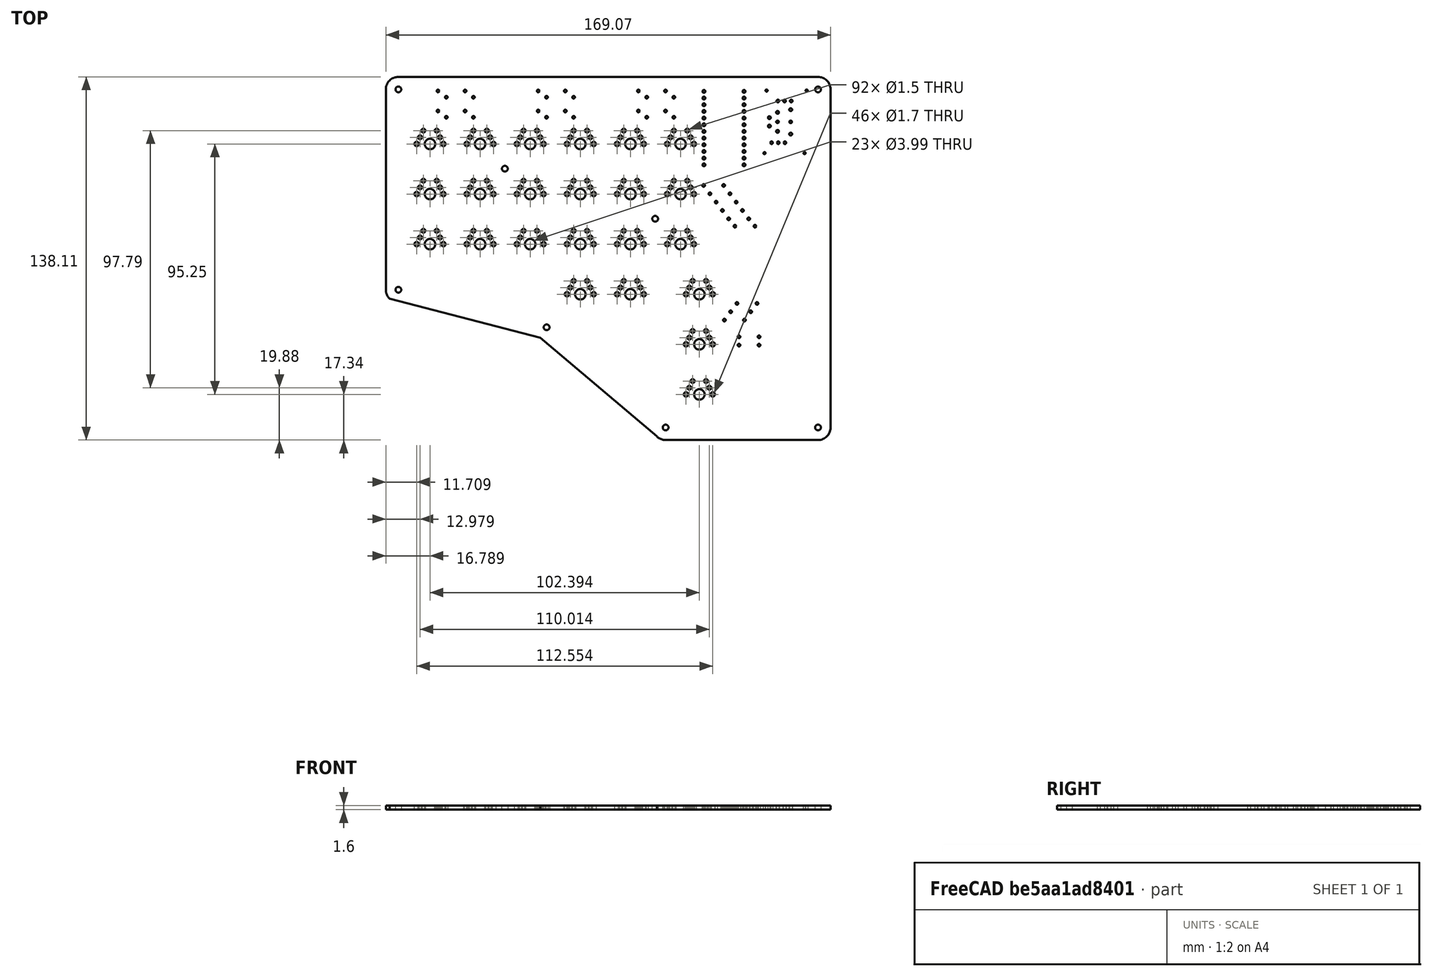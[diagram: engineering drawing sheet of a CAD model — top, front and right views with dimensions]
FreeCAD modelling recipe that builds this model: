
FCSTD DOCUMENT  (FreeCAD 0.19R24267 +148 (Git))
Label: parametric.model.experiment
License: All rights reserved
LicenseURL: http://en.wikipedia.org/wiki/All_rights_reserved
objects: App::Part×4, Sketcher::SketchObject×2, PartDesign::CoordinateSystem×1, Part::Feature×1, PartDesign::Body×1
note: 5 computed .brp shape members not serialized (recipe doc carries the construction recipe); baked Part::Feature solids carry a one-line shape summary decoded from their .brp

FEATURE [PartDesign::CoordinateSystem] Local_CS_c5df
  AttacherType = Attacher::AttachEngine3D
FEATURE [Part::Feature] Pcb_c5df
  Placement = pos=(-21.48,22.9996,0) rot=(0,0,1;0rad)
  shape: bbox 169.1 x 138.1 x 1.6 mm, 270 faces (baked)
FEATURE [Sketcher::SketchObject] PCB_Sketch_c5df
  FullyConstrained = true
  sketch-geometry (11):
    g0: LineSegment StartX=164.25 StartY=2.5e-15 StartZ=0 EndX=164.25 EndY=-128.5 EndZ=0
    g1: LineSegment StartX=54.0843 StartY=-94.6132 StartZ=0 EndX=-1.16741 EndY=-80.6043 EndZ=0
    g2: LineSegment StartX=-4.75 StartY=-1e-15 StartZ=0 EndX=-4.75 EndY=-76 EndZ=0
    g3: LineSegment StartX=-1.3e-15 StartY=4.75 StartZ=0 EndX=159.5 EndY=4.75 EndZ=0
    g4: LineSegment StartX=159.5 StartY=-133.25 StartZ=0 EndX=101.5 EndY=-133.25 EndZ=0
    g5: LineSegment StartX=54.0843 StartY=-94.6132 StartZ=0 EndX=98.4323 EndY=-132.127 EndZ=0
    g6: ArcOfCircle CenterX=0 CenterY=0 CenterZ=0 NormalX=0 NormalY=0 NormalZ=-1 AngleXU=3.25477e-08 Radius=4.75 StartAngle=6.28319 EndAngle=7.85398
    g7: ArcOfCircle CenterX=101.5 CenterY=-128.5 CenterZ=0 NormalX=0 NormalY=0 NormalZ=-1 AngleXU=-1.5708 Radius=4.75 StartAngle=6.28319 EndAngle=6.98529
    g8: ArcOfCircle CenterX=159.5 CenterY=0 CenterZ=0 NormalX=0 NormalY=0 NormalZ=-1 AngleXU=1.5708 Radius=4.75 StartAngle=6.28319 EndAngle=7.85398
    g9: ArcOfCircle CenterX=0 CenterY=-76 CenterZ=0 NormalX=0 NormalY=0 NormalZ=-1 AngleXU=-0.785398 Radius=4.75 StartAngle=5.7461 EndAngle=7.06858
    g10: ArcOfCircle CenterX=159.5 CenterY=-128.5 CenterZ=0 NormalX=0 NormalY=0 NormalZ=-1 AngleXU=-3.14159 Radius=4.75 StartAngle=6.28319 EndAngle=7.85398
  constraints (27):
    c: Coincident(g1,g5)
    c: Tangent(g3,g6) = 1.5708
    c: Horizontal(g3)
    c: Tangent(g3,g8) = 1.5708
    c: Tangent(g0,g8) = 1.5708
    c: Perpendicular(g3,g0)
    c: Tangent(g0,g10) = 1.5708
    c: Tangent(g4,g10) = 1.5708
    c: Tangent(g4,g7) = 1.5708
    c: Tangent(g5,g7) = -1.5708
    c: Perpendicular(g0,g4)
    c: Tangent(g1,g9) = 1.5708
    c: Tangent(g2,g9) = -1.5708
    c: Perpendicular(g3,g2)
    c: Equal(g7,g8)
    c: Equal(g7,g9)
    c: Equal(g7,g10)
    c: Radius(g7) = 4.75
    c: Tangent(g2,g6) = -1.5708
    c: DistanceX(g2,g0) = 169
    c: DistanceY(g4,g3) = 138
    c: DistanceX(g4,g4) = 58
    c: Radius(g6) = 4.75
    c: Coincident(g6,g-1)
    c: DistanceY(g2,g2) = 76
    c: Angle(g1,g5) = 2.68781
    c: Distance(g1) = 57
FEATURE [App::Part] Board_Geoms_c5df
  Group = -> [Local_CS_c5df,Pcb_c5df,PCB_Sketch_c5df]
  Origin = -> Origin
FEATURE [App::Part] Step_Models_c5df
  Origin = -> Origin002
FEATURE [App::Part] Board_c5df  label="pcb"
  Group = -> [Board_Geoms_c5df,Step_Models_c5df]
  Origin = -> Origin001
FEATURE [Sketcher::SketchObject] Sketch003
  FullyConstrained = false
  sketch-geometry (223):
    g0: Circle CenterX=0 CenterY=6e-16 CenterZ=0 NormalX=0 NormalY=0 NormalZ=1 AngleXU=0 Radius=1.1
    g1: Circle CenterX=159.5 CenterY=6e-16 CenterZ=0 NormalX=0 NormalY=0 NormalZ=1 AngleXU=0 Radius=1.1
    g2: LineSegment StartX=3e-16 StartY=4.75 StartZ=0 EndX=159.5 EndY=4.75 EndZ=0
    g3: ArcOfCircle CenterX=159.5 CenterY=-4e-16 CenterZ=0 NormalX=0 NormalY=0 NormalZ=1 AngleXU=0 Radius=4.75 StartAngle=1e-16 EndAngle=1.5708
    g4: LineSegment StartX=164.25 StartY=6e-16 StartZ=0 EndX=164.25 EndY=-128.5 EndZ=0
    g5: Circle CenterX=159.5 CenterY=-128.5 CenterZ=0 NormalX=0 NormalY=0 NormalZ=1 AngleXU=0 Radius=1.1
    g6: ArcOfCircle CenterX=159.5 CenterY=-128.5 CenterZ=0 NormalX=0 NormalY=0 NormalZ=1 AngleXU=0 Radius=4.75 StartAngle=4.71239 EndAngle=6.28319
    g7: LineSegment StartX=159.5 StartY=-133.25 StartZ=0 EndX=101.5 EndY=-133.25 EndZ=0
    g8: Circle CenterX=101.5 CenterY=-128.5 CenterZ=0 NormalX=0 NormalY=0 NormalZ=1 AngleXU=0 Radius=1.1
    g9: ArcOfCircle CenterX=101.5 CenterY=-128.5 CenterZ=0 NormalX=0 NormalY=0 NormalZ=1 AngleXU=0 Radius=4.75 StartAngle=4.01077 EndAngle=4.71239
    g10: LineSegment StartX=98.4341 StartY=-132.128 StartZ=0 EndX=53.9755 EndY=-94.5576 EndZ=0
    g11: LineSegment StartX=53.9755 StartY=-94.5576 StartZ=0 EndX=-1.16521 EndY=-80.6049 EndZ=0
    g12: ArcOfCircle CenterX=9.3e-15 CenterY=-76 CenterZ=0 NormalX=0 NormalY=0 NormalZ=1 AngleXU=0 Radius=4.75 StartAngle=3.14159 EndAngle=4.46455
    g13: LineSegment StartX=-4.75 StartY=-76 StartZ=0 EndX=-4.75 EndY=0 EndZ=0
    g14: LineSegment StartX=5.54 StartY=-13.74 StartZ=0 EndX=18.54 EndY=-13.74 EndZ=0
    g15: LineSegment StartX=5.54 StartY=-27.74 StartZ=0 EndX=18.54 EndY=-27.74 EndZ=0
    g16: LineSegment StartX=5.04 StartY=-14.24 StartZ=0 EndX=5.04 EndY=-27.24 EndZ=0
    g17: LineSegment StartX=19.04 StartY=-14.24 StartZ=0 EndX=19.04 EndY=-27.24 EndZ=0
    g18: ArcOfCircle CenterX=5.54 CenterY=-14.24 CenterZ=0 NormalX=0 NormalY=0 NormalZ=1 AngleXU=0 Radius=0.5 StartAngle=1.5708 EndAngle=3.14159
    g19: ArcOfCircle CenterX=18.54 CenterY=-27.24 CenterZ=0 NormalX=0 NormalY=0 NormalZ=1 AngleXU=0 Radius=0.5 StartAngle=4.71239 EndAngle=6.28319
    g20: LineSegment StartX=24.59 StartY=-13.74 StartZ=0 EndX=37.59 EndY=-13.74 EndZ=0
    g21: LineSegment StartX=24.59 StartY=-27.74 StartZ=0 EndX=37.59 EndY=-27.74 EndZ=0
    g22: LineSegment StartX=24.09 StartY=-14.24 StartZ=0 EndX=24.09 EndY=-27.24 EndZ=0
    g23: LineSegment StartX=38.09 StartY=-14.24 StartZ=0 EndX=38.09 EndY=-27.24 EndZ=0
    g24: ArcOfCircle CenterX=24.59 CenterY=-14.24 CenterZ=0 NormalX=0 NormalY=0 NormalZ=1 AngleXU=0 Radius=0.5 StartAngle=1.5708 EndAngle=3.14159
    g25: ArcOfCircle CenterX=24.59 CenterY=-27.24 CenterZ=0 NormalX=0 NormalY=0 NormalZ=1 AngleXU=0 Radius=0.5 StartAngle=3.14159 EndAngle=4.71239
    g26: LineSegment StartX=5.54 StartY=-32.79 StartZ=0 EndX=18.54 EndY=-32.79 EndZ=0
    g27: LineSegment StartX=5.54 StartY=-46.79 StartZ=0 EndX=18.54 EndY=-46.79 EndZ=0
    g28: LineSegment StartX=5.04 StartY=-33.29 StartZ=0 EndX=5.04 EndY=-46.29 EndZ=0
    g29: LineSegment StartX=19.04 StartY=-33.29 StartZ=0 EndX=19.04 EndY=-46.29 EndZ=0
    g30: ArcOfCircle CenterX=18.54 CenterY=-33.29 CenterZ=0 NormalX=0 NormalY=0 NormalZ=1 AngleXU=0 Radius=0.5 StartAngle=6.341e-13 EndAngle=1.5708
    g31: LineSegment StartX=24.59 StartY=-32.79 StartZ=0 EndX=37.59 EndY=-32.79 EndZ=0
    g32: LineSegment StartX=24.59 StartY=-46.79 StartZ=0 EndX=37.59 EndY=-46.79 EndZ=0
    g33: LineSegment StartX=24.09 StartY=-33.29 StartZ=0 EndX=24.09 EndY=-46.29 EndZ=0
    g34: LineSegment StartX=38.09 StartY=-33.29 StartZ=0 EndX=38.09 EndY=-46.29 EndZ=0
    g35: ArcOfCircle CenterX=24.59 CenterY=-33.29 CenterZ=0 NormalX=0 NormalY=0 NormalZ=1 AngleXU=0 Radius=0.5 StartAngle=1.5708 EndAngle=3.14159
    g36: ArcOfCircle CenterX=37.59 CenterY=-46.29 CenterZ=0 NormalX=0 NormalY=0 NormalZ=1 AngleXU=0 Radius=0.5 StartAngle=4.71239 EndAngle=6.28319
    g37: ArcOfCircle CenterX=18.54 CenterY=-14.24 CenterZ=0 NormalX=0 NormalY=0 NormalZ=1 AngleXU=0 Radius=0.5 StartAngle=9e-16 EndAngle=1.5708
    g38: ArcOfCircle CenterX=37.59 CenterY=-14.24 CenterZ=0 NormalX=0 NormalY=0 NormalZ=1 AngleXU=0 Radius=0.5 StartAngle=-9e-16 EndAngle=1.5708
    g39: ArcOfCircle CenterX=37.59 CenterY=-33.29 CenterZ=0 NormalX=0 NormalY=0 NormalZ=1 AngleXU=0 Radius=0.5 StartAngle=-1.692e-12 EndAngle=1.5708
    g40: ArcOfCircle CenterX=24.59 CenterY=-46.29 CenterZ=0 NormalX=0 NormalY=0 NormalZ=1 AngleXU=0 Radius=0.5 StartAngle=3.14159 EndAngle=4.71239
    g41: ArcOfCircle CenterX=18.54 CenterY=-46.29 CenterZ=0 NormalX=0 NormalY=0 NormalZ=1 AngleXU=0 Radius=0.5 StartAngle=4.71239 EndAngle=6.28319
    g42: ArcOfCircle CenterX=5.54 CenterY=-46.29 CenterZ=0 NormalX=0 NormalY=0 NormalZ=1 AngleXU=0 Radius=0.5 StartAngle=3.14159 EndAngle=4.71239
    g43: ArcOfCircle CenterX=5.54 CenterY=-33.29 CenterZ=0 NormalX=0 NormalY=0 NormalZ=1 AngleXU=0 Radius=0.5 StartAngle=1.5708 EndAngle=3.14159
    g44: ArcOfCircle CenterX=5.54 CenterY=-27.24 CenterZ=0 NormalX=0 NormalY=0 NormalZ=1 AngleXU=0 Radius=0.5 StartAngle=3.14159 EndAngle=4.71239
    g45: LineSegment StartX=43.64 StartY=-13.74 StartZ=0 EndX=56.64 EndY=-13.74 EndZ=0
    g46: LineSegment StartX=43.64 StartY=-27.74 StartZ=0 EndX=56.64 EndY=-27.74 EndZ=0
    g47: LineSegment StartX=43.14 StartY=-14.24 StartZ=0 EndX=43.14 EndY=-27.24 EndZ=0
    g48: LineSegment StartX=57.14 StartY=-14.24 StartZ=0 EndX=57.14 EndY=-27.24 EndZ=0
    g49: ArcOfCircle CenterX=43.64 CenterY=-14.24 CenterZ=0 NormalX=0 NormalY=0 NormalZ=1 AngleXU=0 Radius=0.5 StartAngle=1.5708 EndAngle=3.14159
    g50: ArcOfCircle CenterX=56.64 CenterY=-27.24 CenterZ=0 NormalX=0 NormalY=0 NormalZ=1 AngleXU=0 Radius=0.5 StartAngle=4.71239 EndAngle=6.28319
    g51: LineSegment StartX=62.69 StartY=-13.74 StartZ=0 EndX=75.69 EndY=-13.74 EndZ=0
    g52: LineSegment StartX=62.69 StartY=-27.74 StartZ=0 EndX=75.69 EndY=-27.74 EndZ=0
    g53: LineSegment StartX=62.19 StartY=-14.24 StartZ=0 EndX=62.19 EndY=-27.24 EndZ=0
    g54: LineSegment StartX=76.19 StartY=-14.24 StartZ=0 EndX=76.19 EndY=-27.24 EndZ=0
    g55: ArcOfCircle CenterX=62.69 CenterY=-14.24 CenterZ=0 NormalX=0 NormalY=0 NormalZ=1 AngleXU=0 Radius=0.5 StartAngle=1.5708 EndAngle=3.14159
    g56: ArcOfCircle CenterX=62.69 CenterY=-27.24 CenterZ=0 NormalX=0 NormalY=0 NormalZ=1 AngleXU=0 Radius=0.5 StartAngle=3.14159 EndAngle=4.71239
    g57: LineSegment StartX=43.64 StartY=-32.79 StartZ=0 EndX=56.64 EndY=-32.79 EndZ=0
    g58: LineSegment StartX=43.64 StartY=-46.79 StartZ=0 EndX=56.64 EndY=-46.79 EndZ=0
    g59: LineSegment StartX=43.14 StartY=-33.29 StartZ=0 EndX=43.14 EndY=-46.29 EndZ=0
    g60: LineSegment StartX=57.14 StartY=-33.29 StartZ=0 EndX=57.14 EndY=-46.29 EndZ=0
    g61: ArcOfCircle CenterX=56.64 CenterY=-33.29 CenterZ=0 NormalX=0 NormalY=0 NormalZ=1 AngleXU=0 Radius=0.5 StartAngle=-1.252e-13 EndAngle=1.5708
    g62: LineSegment StartX=62.69 StartY=-32.79 StartZ=0 EndX=75.69 EndY=-32.79 EndZ=0
    g63: LineSegment StartX=62.69 StartY=-46.79 StartZ=0 EndX=75.69 EndY=-46.79 EndZ=0
    g64: LineSegment StartX=62.19 StartY=-33.29 StartZ=0 EndX=62.19 EndY=-46.29 EndZ=0
    g65: LineSegment StartX=76.19 StartY=-33.29 StartZ=0 EndX=76.19 EndY=-46.29 EndZ=0
    g66: ArcOfCircle CenterX=62.69 CenterY=-33.29 CenterZ=0 NormalX=0 NormalY=0 NormalZ=1 AngleXU=0 Radius=0.5 StartAngle=1.5708 EndAngle=3.14159
    g67: ArcOfCircle CenterX=75.69 CenterY=-46.29 CenterZ=0 NormalX=0 NormalY=0 NormalZ=1 AngleXU=0 Radius=0.5 StartAngle=4.71239 EndAngle=6.28319
    g68: ArcOfCircle CenterX=56.64 CenterY=-14.24 CenterZ=0 NormalX=0 NormalY=0 NormalZ=1 AngleXU=0 Radius=0.5 StartAngle=-1.8e-15 EndAngle=1.5708
    g69: ArcOfCircle CenterX=75.69 CenterY=-14.24 CenterZ=0 NormalX=0 NormalY=0 NormalZ=1 AngleXU=0 Radius=0.5 StartAngle=1.8e-15 EndAngle=1.5708
    g70: ArcOfCircle CenterX=75.69 CenterY=-27.24 CenterZ=0 NormalX=0 NormalY=0 NormalZ=1 AngleXU=0 Radius=0.5 StartAngle=4.71239 EndAngle=6.28319
    g71: ArcOfCircle CenterX=75.69 CenterY=-33.29 CenterZ=0 NormalX=0 NormalY=0 NormalZ=1 AngleXU=0 Radius=0.5 StartAngle=0 EndAngle=1.5708
    g72: ArcOfCircle CenterX=62.69 CenterY=-46.29 CenterZ=0 NormalX=0 NormalY=0 NormalZ=1 AngleXU=0 Radius=0.5 StartAngle=3.14159 EndAngle=4.71239
    g73: ArcOfCircle CenterX=56.64 CenterY=-46.29 CenterZ=0 NormalX=0 NormalY=0 NormalZ=1 AngleXU=0 Radius=0.5 StartAngle=4.71239 EndAngle=6.28319
    g74: ArcOfCircle CenterX=43.64 CenterY=-46.29 CenterZ=0 NormalX=0 NormalY=0 NormalZ=1 AngleXU=0 Radius=0.5 StartAngle=3.14159 EndAngle=4.71239
    g75: ArcOfCircle CenterX=43.64 CenterY=-33.29 CenterZ=0 NormalX=0 NormalY=0 NormalZ=1 AngleXU=0 Radius=0.5 StartAngle=1.5708 EndAngle=3.14159
    g76: ArcOfCircle CenterX=43.64 CenterY=-27.24 CenterZ=0 NormalX=0 NormalY=0 NormalZ=1 AngleXU=0 Radius=0.5 StartAngle=3.14159 EndAngle=4.71239
    g77: LineSegment StartX=5.54 StartY=-51.84 StartZ=0 EndX=18.54 EndY=-51.84 EndZ=0
    g78: LineSegment StartX=5.54 StartY=-65.84 StartZ=0 EndX=18.54 EndY=-65.84 EndZ=0
    g79: LineSegment StartX=5.04 StartY=-52.34 StartZ=0 EndX=5.04 EndY=-65.34 EndZ=0
    g80: LineSegment StartX=19.04 StartY=-52.34 StartZ=0 EndX=19.04 EndY=-65.34 EndZ=0
    g81: ArcOfCircle CenterX=18.54 CenterY=-52.34 CenterZ=0 NormalX=0 NormalY=0 NormalZ=1 AngleXU=0 Radius=0.5 StartAngle=1.38282e-07 EndAngle=1.5708
    g82: LineSegment StartX=24.59 StartY=-51.84 StartZ=0 EndX=37.59 EndY=-51.84 EndZ=0
    g83: LineSegment StartX=24.59 StartY=-65.84 StartZ=0 EndX=37.59 EndY=-65.84 EndZ=0
    g84: LineSegment StartX=24.09 StartY=-52.34 StartZ=0 EndX=24.09 EndY=-65.34 EndZ=0
    g85: LineSegment StartX=38.09 StartY=-52.34 StartZ=0 EndX=38.09 EndY=-65.34 EndZ=0
    g86: ArcOfCircle CenterX=37.59 CenterY=-65.34 CenterZ=0 NormalX=0 NormalY=0 NormalZ=1 AngleXU=0 Radius=0.5 StartAngle=4.71239 EndAngle=6.28319
    g87: ArcOfCircle CenterX=24.59 CenterY=-65.34 CenterZ=0 NormalX=0 NormalY=0 NormalZ=1 AngleXU=0 Radius=0.5 StartAngle=3.14159 EndAngle=4.71239
    g88: ArcOfCircle CenterX=18.54 CenterY=-65.34 CenterZ=0 NormalX=0 NormalY=0 NormalZ=1 AngleXU=0 Radius=0.5 StartAngle=4.71239 EndAngle=6.28317
    g89: ArcOfCircle CenterX=5.54 CenterY=-65.34 CenterZ=0 NormalX=0 NormalY=0 NormalZ=1 AngleXU=0 Radius=0.5 StartAngle=3.14161 EndAngle=4.71239
    g90: ArcOfCircle CenterX=5.54 CenterY=-52.34 CenterZ=0 NormalX=0 NormalY=0 NormalZ=1 AngleXU=0 Radius=0.5 StartAngle=1.5708 EndAngle=3.14159
    g91: LineSegment StartX=43.64 StartY=-51.84 StartZ=0 EndX=56.64 EndY=-51.84 EndZ=0
    g92: LineSegment StartX=43.64 StartY=-65.84 StartZ=0 EndX=56.64 EndY=-65.84 EndZ=0
    g93: LineSegment StartX=43.14 StartY=-52.34 StartZ=0 EndX=43.14 EndY=-65.34 EndZ=0
    g94: LineSegment StartX=57.14 StartY=-52.34 StartZ=0 EndX=57.14 EndY=-65.34 EndZ=0
    g95: ArcOfCircle CenterX=56.64 CenterY=-52.34 CenterZ=0 NormalX=0 NormalY=0 NormalZ=1 AngleXU=0 Radius=0.5 StartAngle=1.73068e-05 EndAngle=1.5708
    g96: LineSegment StartX=62.69 StartY=-51.84 StartZ=0 EndX=75.69 EndY=-51.84 EndZ=0
    g97: LineSegment StartX=62.69 StartY=-65.84 StartZ=0 EndX=75.69 EndY=-65.84 EndZ=0
    g98: LineSegment StartX=62.19 StartY=-52.34 StartZ=0 EndX=62.19 EndY=-65.34 EndZ=0
    g99: LineSegment StartX=76.19 StartY=-52.34 StartZ=0 EndX=76.19 EndY=-65.34 EndZ=0
    g100: ArcOfCircle CenterX=62.69 CenterY=-52.34 CenterZ=0 NormalX=0 NormalY=0 NormalZ=1 AngleXU=0 Radius=0.5 StartAngle=1.5708 EndAngle=3.14158
    g101: ArcOfCircle CenterX=75.69 CenterY=-65.34 CenterZ=0 NormalX=0 NormalY=0 NormalZ=1 AngleXU=0 Radius=0.5 StartAngle=4.71239 EndAngle=6.28317
    g102: ArcOfCircle CenterX=62.69 CenterY=-65.34 CenterZ=0 NormalX=0 NormalY=0 NormalZ=1 AngleXU=0 Radius=0.5 StartAngle=3.14159 EndAngle=4.71239
    g103: ArcOfCircle CenterX=56.64 CenterY=-65.34 CenterZ=0 NormalX=0 NormalY=0 NormalZ=1 AngleXU=0 Radius=0.5 StartAngle=4.71239 EndAngle=6.28319
    g104: ArcOfCircle CenterX=43.64 CenterY=-65.34 CenterZ=0 NormalX=0 NormalY=0 NormalZ=1 AngleXU=0 Radius=0.5 StartAngle=3.14159 EndAngle=4.71239
    g105: ArcOfCircle CenterX=43.64 CenterY=-52.34 CenterZ=0 NormalX=0 NormalY=0 NormalZ=1 AngleXU=0 Radius=0.5 StartAngle=1.5708 EndAngle=3.14158
    g106: ArcOfCircle CenterX=24.59 CenterY=-52.34 CenterZ=0 NormalX=0 NormalY=0 NormalZ=1 AngleXU=0 Radius=0.5 StartAngle=1.5708 EndAngle=3.14158
    g107: ArcOfCircle CenterX=37.59 CenterY=-52.34 CenterZ=0 NormalX=0 NormalY=0 NormalZ=1 AngleXU=0 Radius=0.5 StartAngle=1.73068e-05 EndAngle=1.5708
    g108: LineSegment StartX=81.74 StartY=-13.74 StartZ=0 EndX=94.74 EndY=-13.74 EndZ=0
    g109: LineSegment StartX=81.74 StartY=-27.74 StartZ=0 EndX=94.74 EndY=-27.74 EndZ=0
    g110: LineSegment StartX=81.24 StartY=-14.24 StartZ=0 EndX=81.24 EndY=-27.24 EndZ=0
    g111: LineSegment StartX=95.24 StartY=-14.24 StartZ=0 EndX=95.24 EndY=-27.24 EndZ=0
    g112: ArcOfCircle CenterX=81.74 CenterY=-14.24 CenterZ=0 NormalX=0 NormalY=0 NormalZ=1 AngleXU=0 Radius=0.5 StartAngle=1.5708 EndAngle=3.14159
    g113: ArcOfCircle CenterX=94.74 CenterY=-27.24 CenterZ=0 NormalX=0 NormalY=0 NormalZ=1 AngleXU=0 Radius=0.5 StartAngle=4.71239 EndAngle=6.28319
    g114: LineSegment StartX=100.79 StartY=-13.74 StartZ=0 EndX=113.79 EndY=-13.74 EndZ=0
    g115: LineSegment StartX=100.79 StartY=-27.74 StartZ=0 EndX=113.79 EndY=-27.74 EndZ=0
    g116: LineSegment StartX=100.29 StartY=-14.24 StartZ=0 EndX=100.29 EndY=-27.24 EndZ=0
    g117: LineSegment StartX=114.29 StartY=-14.24 StartZ=0 EndX=114.29 EndY=-27.24 EndZ=0
    g118: ArcOfCircle CenterX=100.79 CenterY=-14.24 CenterZ=0 NormalX=0 NormalY=0 NormalZ=1 AngleXU=0 Radius=0.5 StartAngle=1.5708 EndAngle=3.14159
    g119: ArcOfCircle CenterX=100.79 CenterY=-27.24 CenterZ=0 NormalX=0 NormalY=0 NormalZ=1 AngleXU=0 Radius=0.5 StartAngle=3.14159 EndAngle=4.71239
    g120: LineSegment StartX=81.74 StartY=-32.79 StartZ=0 EndX=94.74 EndY=-32.79 EndZ=0
    g121: LineSegment StartX=81.74 StartY=-46.79 StartZ=0 EndX=94.74 EndY=-46.79 EndZ=0
    g122: LineSegment StartX=81.24 StartY=-33.29 StartZ=0 EndX=81.24 EndY=-46.29 EndZ=0
    g123: LineSegment StartX=95.24 StartY=-33.29 StartZ=0 EndX=95.24 EndY=-46.29 EndZ=0
    g124: ArcOfCircle CenterX=94.74 CenterY=-33.29 CenterZ=0 NormalX=0 NormalY=0 NormalZ=1 AngleXU=0 Radius=0.5 StartAngle=-9e-16 EndAngle=1.5708
    g125: LineSegment StartX=100.79 StartY=-32.79 StartZ=0 EndX=113.79 EndY=-32.79 EndZ=0
    g126: LineSegment StartX=100.79 StartY=-46.79 StartZ=0 EndX=113.79 EndY=-46.79 EndZ=0
    g127: LineSegment StartX=100.29 StartY=-33.29 StartZ=0 EndX=100.29 EndY=-46.29 EndZ=0
    g128: LineSegment StartX=114.29 StartY=-33.29 StartZ=0 EndX=114.29 EndY=-46.29 EndZ=0
    g129: ArcOfCircle CenterX=100.79 CenterY=-33.29 CenterZ=0 NormalX=0 NormalY=0 NormalZ=1 AngleXU=0 Radius=0.5 StartAngle=1.5708 EndAngle=3.14159
    g130: ArcOfCircle CenterX=113.79 CenterY=-46.29 CenterZ=0 NormalX=0 NormalY=0 NormalZ=1 AngleXU=0 Radius=0.5 StartAngle=4.71239 EndAngle=6.28319
    g131: ArcOfCircle CenterX=94.74 CenterY=-14.24 CenterZ=0 NormalX=0 NormalY=0 NormalZ=1 AngleXU=0 Radius=0.5 StartAngle=2e-16 EndAngle=1.5708
    g132: ArcOfCircle CenterX=113.79 CenterY=-14.24 CenterZ=0 NormalX=0 NormalY=0 NormalZ=1 AngleXU=0 Radius=0.5 StartAngle=0 EndAngle=1.5708
    g133: ArcOfCircle CenterX=113.79 CenterY=-27.24 CenterZ=0 NormalX=0 NormalY=0 NormalZ=1 AngleXU=0 Radius=0.5 StartAngle=4.71239 EndAngle=6.28319
    g134: ArcOfCircle CenterX=113.79 CenterY=-33.29 CenterZ=0 NormalX=0 NormalY=0 NormalZ=1 AngleXU=0 Radius=0.5 StartAngle=-2.7e-15 EndAngle=1.5708
    g135: ArcOfCircle CenterX=100.79 CenterY=-46.29 CenterZ=0 NormalX=0 NormalY=0 NormalZ=1 AngleXU=0 Radius=0.5 StartAngle=3.14159 EndAngle=4.71239
    g136: ArcOfCircle CenterX=94.74 CenterY=-46.29 CenterZ=0 NormalX=0 NormalY=0 NormalZ=1 AngleXU=0 Radius=0.5 StartAngle=4.71239 EndAngle=6.28319
    g137: ArcOfCircle CenterX=81.74 CenterY=-46.29 CenterZ=0 NormalX=0 NormalY=0 NormalZ=1 AngleXU=0 Radius=0.5 StartAngle=3.14159 EndAngle=4.71239
    g138: ArcOfCircle CenterX=81.74 CenterY=-33.29 CenterZ=0 NormalX=0 NormalY=0 NormalZ=1 AngleXU=0 Radius=0.5 StartAngle=1.5708 EndAngle=3.14159
    g139: ArcOfCircle CenterX=81.74 CenterY=-27.24 CenterZ=0 NormalX=0 NormalY=0 NormalZ=1 AngleXU=0 Radius=0.5 StartAngle=3.14159 EndAngle=4.71239
    g140: LineSegment StartX=81.74 StartY=-51.84 StartZ=0 EndX=94.74 EndY=-51.84 EndZ=0
    g141: LineSegment StartX=81.74 StartY=-65.84 StartZ=0 EndX=94.74 EndY=-65.84 EndZ=0
    g142: LineSegment StartX=81.24 StartY=-52.34 StartZ=0 EndX=81.24 EndY=-65.34 EndZ=0
    g143: LineSegment StartX=95.24 StartY=-52.34 StartZ=0 EndX=95.24 EndY=-65.34 EndZ=0
    g144: ArcOfCircle CenterX=94.74 CenterY=-52.34 CenterZ=0 NormalX=0 NormalY=0 NormalZ=1 AngleXU=0 Radius=0.5 StartAngle=1.4259e-07 EndAngle=1.5708
    g145: LineSegment StartX=100.79 StartY=-51.84 StartZ=0 EndX=113.79 EndY=-51.84 EndZ=0
    g146: LineSegment StartX=100.79 StartY=-65.84 StartZ=0 EndX=113.79 EndY=-65.84 EndZ=0
    g147: LineSegment StartX=100.29 StartY=-52.34 StartZ=0 EndX=100.29 EndY=-65.34 EndZ=0
    g148: LineSegment StartX=114.29 StartY=-52.34 StartZ=0 EndX=114.29 EndY=-65.34 EndZ=0
    g149: ArcOfCircle CenterX=100.79 CenterY=-52.34 CenterZ=0 NormalX=0 NormalY=0 NormalZ=1 AngleXU=0 Radius=0.5 StartAngle=1.5708 EndAngle=3.14161
    g150: ArcOfCircle CenterX=113.79 CenterY=-65.34 CenterZ=0 NormalX=0 NormalY=0 NormalZ=1 AngleXU=0 Radius=0.5 StartAngle=4.71239 EndAngle=6.2832
    g151: ArcOfCircle CenterX=100.79 CenterY=-65.34 CenterZ=0 NormalX=0 NormalY=0 NormalZ=1 AngleXU=0 Radius=0.5 StartAngle=3.14163 EndAngle=4.71239
    g152: ArcOfCircle CenterX=94.74 CenterY=-65.34 CenterZ=0 NormalX=0 NormalY=0 NormalZ=1 AngleXU=0 Radius=0.5 StartAngle=4.71239 EndAngle=6.28317
    g153: ArcOfCircle CenterX=81.74 CenterY=-65.34 CenterZ=0 NormalX=0 NormalY=0 NormalZ=1 AngleXU=0 Radius=0.5 StartAngle=3.14161 EndAngle=4.71239
    g154: LineSegment StartX=62.69 StartY=-70.89 StartZ=0 EndX=75.69 EndY=-70.89 EndZ=0
    g155: LineSegment StartX=62.69 StartY=-84.89 StartZ=0 EndX=75.69 EndY=-84.89 EndZ=0
    g156: LineSegment StartX=62.19 StartY=-71.39 StartZ=0 EndX=62.19 EndY=-84.39 EndZ=0
    g157: LineSegment StartX=76.19 StartY=-71.39 StartZ=0 EndX=76.19 EndY=-84.39 EndZ=0
    g158: ArcOfCircle CenterX=62.69 CenterY=-71.39 CenterZ=0 NormalX=0 NormalY=0 NormalZ=1 AngleXU=0 Radius=0.5 StartAngle=1.5708 EndAngle=3.14159
    g159: ArcOfCircle CenterX=75.69 CenterY=-84.39 CenterZ=0 NormalX=0 NormalY=0 NormalZ=1 AngleXU=0 Radius=0.5 StartAngle=4.71239 EndAngle=6.28319
    g160: ArcOfCircle CenterX=75.69 CenterY=-71.39 CenterZ=0 NormalX=0 NormalY=0 NormalZ=1 AngleXU=0 Radius=0.5 StartAngle=4.1638e-12 EndAngle=1.5708
    g161: ArcOfCircle CenterX=62.69 CenterY=-84.39 CenterZ=0 NormalX=0 NormalY=0 NormalZ=1 AngleXU=0 Radius=0.5 StartAngle=3.14159 EndAngle=4.71239
    g162: LineSegment StartX=81.74 StartY=-70.89 StartZ=0 EndX=94.74 EndY=-70.89 EndZ=0
    g163: LineSegment StartX=81.74 StartY=-84.89 StartZ=0 EndX=94.74 EndY=-84.89 EndZ=0
    g164: LineSegment StartX=81.24 StartY=-71.39 StartZ=0 EndX=81.24 EndY=-84.39 EndZ=0
    g165: LineSegment StartX=95.24 StartY=-71.39 StartZ=0 EndX=95.24 EndY=-84.39 EndZ=0
    g166: ArcOfCircle CenterX=94.74 CenterY=-71.39 CenterZ=0 NormalX=0 NormalY=0 NormalZ=1 AngleXU=0 Radius=0.5 StartAngle=6.3e-15 EndAngle=1.5708
    g167: ArcOfCircle CenterX=94.74 CenterY=-84.39 CenterZ=0 NormalX=0 NormalY=0 NormalZ=1 AngleXU=0 Radius=0.5 StartAngle=4.71239 EndAngle=6.28319
    g168: ArcOfCircle CenterX=81.74 CenterY=-84.39 CenterZ=0 NormalX=0 NormalY=0 NormalZ=1 AngleXU=0 Radius=0.5 StartAngle=3.14159 EndAngle=4.71239
    g169: ArcOfCircle CenterX=81.74 CenterY=-71.39 CenterZ=0 NormalX=0 NormalY=0 NormalZ=1 AngleXU=0 Radius=0.5 StartAngle=1.5708 EndAngle=3.14159
    g170: ArcOfCircle CenterX=125.68 CenterY=-84.39 CenterZ=0 NormalX=0 NormalY=0 NormalZ=1 AngleXU=0 Radius=0.5 StartAngle=4.71239 EndAngle=6.28319
    g171: LineSegment StartX=126.18 StartY=-71.39 StartZ=0 EndX=126.18 EndY=-84.39 EndZ=0
    g172: LineSegment StartX=124.68 StartY=-84.89 StartZ=0 EndX=125.68 EndY=-84.89 EndZ=0
    g173: ArcOfCircle CenterX=124.68 CenterY=-84.39 CenterZ=0 NormalX=0 NormalY=0 NormalZ=1 AngleXU=0 Radius=0.5 StartAngle=3.14159 EndAngle=4.71239
    g174: LineSegment StartX=124.18 StartY=-71.39 StartZ=0 EndX=124.18 EndY=-84.39 EndZ=0
    g175: LineSegment StartX=121.43 StartY=-71.39 StartZ=0 EndX=121.43 EndY=-84.39 EndZ=0
    g176: ArcOfCircle CenterX=120.93 CenterY=-84.39 CenterZ=0 NormalX=0 NormalY=0 NormalZ=1 AngleXU=0 Radius=0.5 StartAngle=4.71239 EndAngle=6.28319
    g177: LineSegment StartX=107.93 StartY=-84.89 StartZ=0 EndX=120.93 EndY=-84.89 EndZ=0
    g178: ArcOfCircle CenterX=107.93 CenterY=-84.39 CenterZ=0 NormalX=0 NormalY=0 NormalZ=1 AngleXU=0 Radius=0.5 StartAngle=3.14159 EndAngle=4.71239
    g179: LineSegment StartX=107.43 StartY=-71.39 StartZ=0 EndX=107.43 EndY=-84.39 EndZ=0
    g180: LineSegment StartX=104.68 StartY=-71.39 StartZ=0 EndX=104.68 EndY=-84.39 EndZ=0
    g181: ArcOfCircle CenterX=104.18 CenterY=-84.39 CenterZ=0 NormalX=0 NormalY=0 NormalZ=1 AngleXU=0 Radius=0.5 StartAngle=4.71239 EndAngle=6.28319
    g182: LineSegment StartX=103.18 StartY=-84.89 StartZ=0 EndX=104.18 EndY=-84.89 EndZ=0
    g183: ArcOfCircle CenterX=103.18 CenterY=-84.39 CenterZ=0 NormalX=0 NormalY=0 NormalZ=1 AngleXU=0 Radius=0.5 StartAngle=3.14159 EndAngle=4.71239
    g184: LineSegment StartX=102.68 StartY=-71.39 StartZ=0 EndX=102.68 EndY=-84.39 EndZ=0
    g185: ArcOfCircle CenterX=125.68 CenterY=-71.39 CenterZ=0 NormalX=0 NormalY=0 NormalZ=1 AngleXU=0 Radius=0.5 StartAngle=3.35e-14 EndAngle=1.5708
    g186: LineSegment StartX=124.68 StartY=-70.89 StartZ=0 EndX=125.68 EndY=-70.89 EndZ=0
    g187: ArcOfCircle CenterX=124.68 CenterY=-71.39 CenterZ=0 NormalX=0 NormalY=0 NormalZ=1 AngleXU=0 Radius=0.5 StartAngle=1.5708 EndAngle=3.14159
    g188: ArcOfCircle CenterX=120.93 CenterY=-71.39 CenterZ=0 NormalX=0 NormalY=0 NormalZ=1 AngleXU=0 Radius=0.5 StartAngle=3.279e-13 EndAngle=1.5708
    g189: LineSegment StartX=107.93 StartY=-70.89 StartZ=0 EndX=120.93 EndY=-70.89 EndZ=0
    g190: ArcOfCircle CenterX=107.93 CenterY=-71.39 CenterZ=0 NormalX=0 NormalY=0 NormalZ=1 AngleXU=0 Radius=0.5 StartAngle=1.5708 EndAngle=3.14159
    g191: ArcOfCircle CenterX=104.18 CenterY=-71.39 CenterZ=0 NormalX=0 NormalY=0 NormalZ=1 AngleXU=0 Radius=0.5 StartAngle=3.257e-13 EndAngle=1.5708
    g192: LineSegment StartX=103.18 StartY=-70.89 StartZ=0 EndX=104.18 EndY=-70.89 EndZ=0
    g193: ArcOfCircle CenterX=103.18 CenterY=-71.39 CenterZ=0 NormalX=0 NormalY=0 NormalZ=1 AngleXU=0 Radius=0.5 StartAngle=1.5708 EndAngle=3.14159
    g194: ArcOfCircle CenterX=113.79 CenterY=-52.34 CenterZ=0 NormalX=0 NormalY=0 NormalZ=1 AngleXU=0 Radius=0.5 StartAngle=3.47156e-05 EndAngle=1.5708
    g195: ArcOfCircle CenterX=125.68 CenterY=-103.44 CenterZ=0 NormalX=0 NormalY=0 NormalZ=1 AngleXU=0 Radius=0.5 StartAngle=4.71239 EndAngle=6.28319
    g196: LineSegment StartX=126.18 StartY=-90.44 StartZ=0 EndX=126.18 EndY=-103.44 EndZ=0
    g197: LineSegment StartX=124.68 StartY=-103.94 StartZ=0 EndX=125.68 EndY=-103.94 EndZ=0
    g198: ArcOfCircle CenterX=124.68 CenterY=-103.44 CenterZ=0 NormalX=0 NormalY=0 NormalZ=1 AngleXU=0 Radius=0.5 StartAngle=3.14159 EndAngle=4.71239
    g199: LineSegment StartX=124.18 StartY=-90.44 StartZ=0 EndX=124.18 EndY=-103.44 EndZ=0
    g200: LineSegment StartX=121.43 StartY=-90.44 StartZ=0 EndX=121.43 EndY=-103.44 EndZ=0
    g201: ArcOfCircle CenterX=120.93 CenterY=-103.44 CenterZ=0 NormalX=0 NormalY=0 NormalZ=1 AngleXU=0 Radius=0.5 StartAngle=4.71239 EndAngle=6.28319
    g202: LineSegment StartX=107.93 StartY=-103.94 StartZ=0 EndX=120.93 EndY=-103.94 EndZ=0
    g203: ArcOfCircle CenterX=107.93 CenterY=-103.44 CenterZ=0 NormalX=0 NormalY=0 NormalZ=1 AngleXU=0 Radius=0.5 StartAngle=3.14159 EndAngle=4.71239
    g204: LineSegment StartX=107.43 StartY=-90.44 StartZ=0 EndX=107.43 EndY=-103.44 EndZ=0
    g205: LineSegment StartX=104.68 StartY=-90.44 StartZ=0 EndX=104.68 EndY=-103.44 EndZ=0
    g206: ArcOfCircle CenterX=104.18 CenterY=-103.44 CenterZ=0 NormalX=0 NormalY=0 NormalZ=1 AngleXU=0 Radius=0.5 StartAngle=4.71239 EndAngle=6.28319
    g207: LineSegment StartX=103.18 StartY=-103.94 StartZ=0 EndX=104.18 EndY=-103.94 EndZ=0
    g208: ArcOfCircle CenterX=103.18 CenterY=-103.44 CenterZ=0 NormalX=0 NormalY=0 NormalZ=1 AngleXU=0 Radius=0.5 StartAngle=3.14159 EndAngle=4.71239
    g209: LineSegment StartX=102.68 StartY=-90.44 StartZ=0 EndX=102.68 EndY=-103.44 EndZ=0
    g210: ArcOfCircle CenterX=125.68 CenterY=-90.44 CenterZ=0 NormalX=0 NormalY=0 NormalZ=1 AngleXU=0 Radius=0.5 StartAngle=1.4e-14 EndAngle=1.5708
    g211: LineSegment StartX=124.68 StartY=-89.94 StartZ=0 EndX=125.68 EndY=-89.94 EndZ=0
    g212: ArcOfCircle CenterX=124.68 CenterY=-90.44 CenterZ=0 NormalX=0 NormalY=0 NormalZ=1 AngleXU=0 Radius=0.5 StartAngle=1.5708 EndAngle=3.14159
    g213: ArcOfCircle CenterX=120.93 CenterY=-90.44 CenterZ=0 NormalX=0 NormalY=0 NormalZ=1 AngleXU=0 Radius=0.5 StartAngle=2.9e-15 EndAngle=1.5708
    g214: LineSegment StartX=107.93 StartY=-89.94 StartZ=0 EndX=120.93 EndY=-89.94 EndZ=0
    g215: ArcOfCircle CenterX=107.93 CenterY=-90.44 CenterZ=0 NormalX=0 NormalY=0 NormalZ=1 AngleXU=0 Radius=0.5 StartAngle=1.5708 EndAngle=3.14159
    g216: ArcOfCircle CenterX=104.18 CenterY=-90.44 CenterZ=0 NormalX=0 NormalY=0 NormalZ=1 AngleXU=0 Radius=0.5 StartAngle=6.5e-15 EndAngle=1.5708
    g217: LineSegment StartX=103.18 StartY=-89.94 StartZ=0 EndX=104.18 EndY=-89.94 EndZ=0
    g218: ArcOfCircle CenterX=103.18 CenterY=-90.44 CenterZ=0 NormalX=0 NormalY=0 NormalZ=1 AngleXU=0 Radius=0.5 StartAngle=1.5708 EndAngle=3.14159
    g219: ArcOfCircle CenterX=75.69 CenterY=-52.34 CenterZ=0 NormalX=0 NormalY=0 NormalZ=1 AngleXU=0 Radius=0.5 StartAngle=3.51198e-06 EndAngle=1.5708
    g220: ArcOfCircle CenterX=81.74 CenterY=-52.34 CenterZ=0 NormalX=0 NormalY=0 NormalZ=1 AngleXU=0 Radius=0.5 StartAngle=1.5708 EndAngle=3.14159
    g221: ArcOfCircle CenterX=37.59 CenterY=-27.24 CenterZ=0 NormalX=0 NormalY=0 NormalZ=1 AngleXU=0 Radius=0.5 StartAngle=4.71239 EndAngle=6.28319
    g222: ArcOfCircle CenterX=0 CenterY=6e-16 CenterZ=0 NormalX=0 NormalY=0 NormalZ=1 AngleXU=0 Radius=4.75 StartAngle=1.5708 EndAngle=3.14159
  constraints (620):
    c: Coincident(g0,g222)
    c: Coincident(g0,g-1)
    c: Coincident(g28,g43)
    c: Coincident(g26,g43)
    c: Coincident(g26,g30)
    c: Coincident(g29,g30)
    c: Coincident(g33,g35)
    c: Coincident(g31,g35)
    c: Coincident(g31,g39)
    c: Coincident(g34,g39)
    c: Coincident(g59,g75)
    c: Coincident(g57,g75)
    c: Coincident(g57,g61)
    c: Coincident(g60,g61)
    c: Coincident(g123,g136)
    c: Coincident(g121,g136)
    c: Coincident(g121,g137)
    c: Coincident(g122,g137)
    c: Coincident(g65,g67)
    c: Coincident(g63,g67)
    c: Coincident(g63,g72)
    c: Coincident(g60,g73)
    c: Coincident(g58,g73)
    c: Coincident(g58,g74)
    c: Coincident(g59,g74)
    c: Coincident(g34,g36)
    c: Coincident(g32,g36)
    c: Coincident(g32,g40)
    c: Coincident(g33,g40)
    c: Coincident(g29,g41)
    c: Coincident(g27,g41)
    c: Coincident(g27,g42)
    c: Coincident(g28,g42)
    c: Coincident(g79,g90)
    c: Coincident(g77,g90)
    c: Coincident(g77,g81)
    c: Coincident(g80,g81)
    c: Coincident(g84,g106)
    c: Coincident(g82,g106)
    c: Coincident(g82,g107)
    c: Coincident(g85,g107)
    c: Coincident(g93,g105)
    c: Coincident(g91,g105)
    c: Coincident(g91,g95)
    c: Coincident(g94,g95)
    c: Coincident(g98,g100)
    c: Coincident(g96,g100)
    c: Coincident(g96,g219)
    c: Coincident(g99,g219)
    c: Coincident(g142,g220)
    c: Coincident(g140,g220)
    c: Coincident(g140,g144)
    c: Coincident(g143,g144)
    c: Coincident(g147,g149)
    c: Coincident(g145,g149)
    c: Coincident(g145,g194)
    c: Coincident(g148,g194)
    c: Coincident(g148,g150)
    c: Coincident(g146,g150)
    c: Coincident(g146,g151)
    c: Coincident(g147,g151)
    c: Coincident(g143,g152)
    c: Coincident(g141,g152)
    c: Coincident(g141,g153)
    c: Coincident(g142,g153)
    c: Coincident(g99,g101)
    c: Coincident(g97,g101)
    c: Coincident(g97,g102)
    c: Coincident(g98,g102)
    c: Coincident(g94,g103)
    c: Coincident(g92,g103)
    c: Coincident(g92,g104)
    c: Coincident(g93,g104)
    c: Coincident(g85,g86)
    c: Coincident(g83,g86)
    c: Coincident(g83,g87)
    c: Coincident(g84,g87)
    c: Coincident(g80,g88)
    c: Coincident(g78,g88)
    c: Coincident(g78,g89)
    c: Coincident(g79,g89)
    c: Coincident(g156,g158)
    c: Coincident(g154,g158)
    c: Coincident(g154,g160)
    c: Coincident(g157,g160)
    c: Coincident(g164,g169)
    c: Coincident(g162,g169)
    c: Coincident(g162,g166)
    c: Coincident(g165,g166)
    c: Coincident(g184,g193)
    c: Coincident(g192,g193)
    c: Coincident(g191,g192)
    c: Coincident(g180,g191)
    c: Coincident(g179,g190)
    c: Coincident(g189,g190)
    c: Coincident(g188,g189)
    c: Coincident(g175,g188)
    c: Coincident(g174,g187)
    c: Coincident(g186,g187)
    c: Coincident(g185,g186)
    c: Coincident(g171,g185)
    c: Coincident(g170,g171)
    c: Coincident(g170,g172)
    c: Coincident(g172,g173)
    c: Coincident(g173,g174)
    c: Coincident(g175,g176)
    c: Coincident(g176,g177)
    c: Coincident(g177,g178)
    c: Coincident(g178,g179)
    c: Coincident(g180,g181)
    c: Coincident(g181,g182)
    c: Coincident(g182,g183)
    c: Coincident(g183,g184)
    c: Coincident(g165,g167)
    c: Coincident(g163,g167)
    c: Coincident(g163,g168)
    c: Coincident(g164,g168)
    c: Coincident(g157,g159)
    c: Coincident(g155,g159)
    c: Coincident(g155,g161)
    c: Coincident(g156,g161)
    c: Coincident(g209,g218)
    c: Coincident(g217,g218)
    c: Coincident(g216,g217)
    c: Coincident(g205,g216)
    c: Coincident(g204,g215)
    c: Coincident(g214,g215)
    c: Coincident(g213,g214)
    c: Coincident(g200,g213)
    c: Coincident(g199,g212)
    c: Coincident(g211,g212)
    c: Coincident(g210,g211)
    c: Coincident(g196,g210)
    c: Coincident(g195,g196)
    c: Coincident(g195,g197)
    c: Coincident(g197,g198)
    c: Coincident(g198,g199)
    c: Coincident(g200,g201)
    c: Coincident(g201,g202)
    c: Coincident(g202,g203)
    c: Coincident(g203,g204)
    c: Coincident(g205,g206)
    c: Coincident(g206,g207)
    c: Coincident(g207,g208)
    c: Coincident(g208,g209)
    c: Coincident(g3,g4)
    c: Horizontal(g3,g1)
    c: Horizontal(g1,g0)
    c: Horizontal(g0,g13)
    c: Coincident(g6,g7)
    c: Horizontal(g4,g5)
    c: Vertical(g6,g5)
    c: Vertical(g5,g1)
    c: Vertical(g1,g2)
    c: Coincident(g10,g11)
    c: Radius(g0) = 1.1
    c: Equal(g0,g1)
    c: Equal(g1,g5)
    c: Equal(g5,g8)
    c: Equal(g222,g3)
    c: Equal(g3,g6)
    c: Tangent(g2,g222) = 1.5708
    c: Tangent(g13,g222) = 1.5708
    c: Horizontal(g2)
    c: Vertical(g4)
    c: DistanceX(g13,g3) = 169
    c: Tangent(g2,g3) = 1.5708
    c: DistanceY(g6,g2) = 138
    c: Tangent(g4,g6) = 1.5708
    c: Tangent(g7,g9) = 1.5708
    c: Coincident(g8,g9)
    c: DistanceX(g8,g5) = 58
    c: Vertical(g7,g8)
    c: Horizontal(g9,g5)
    c: Tangent(g9,g10) = 1.5708
    c: DistanceY(g12,g0) = 76
    c: Tangent(g12,g13) = 1.5708
    c: Tangent(g11,g12) = 1.5708
    c: Radius(g12) = 4.75
    c: Angle(g11,g10) = 2.68781
    c: Angle(g7,g10) = 2.43997
    c: DistanceX(g0,g16) = 5.04
    c: DistanceY(g14,g0) = 13.74
    c: Radius(g18) = 0.5
    c: Tangent(g16,g18) = -1.5708
    c: Tangent(g14,g18) = 1.5708
    c: Horizontal(g14)
    c: Horizontal(g20)
    c: Horizontal(g45)
    c: Horizontal(g51)
    c: Horizontal(g108)
    c: Horizontal(g114)
    c: Horizontal(g115)
    c: Horizontal(g109)
    c: Horizontal(g52)
    c: Horizontal(g46)
    c: Horizontal(g21)
    c: Horizontal(g15)
    c: Horizontal(g26)
    c: Horizontal(g27)
    c: Horizontal(g32)
    c: Horizontal(g31)
    c: Horizontal(g57)
    c: Horizontal(g58)
    c: Horizontal(g62)
    c: Horizontal(g63)
    c: Horizontal(g121)
    c: Horizontal(g120)
    c: Horizontal(g125)
    c: Horizontal(g126)
    c: Horizontal(g145)
    c: Horizontal(g146)
    c: Horizontal(g141)
    c: Horizontal(g140)
    c: Horizontal(g96)
    c: Horizontal(g97)
    c: Horizontal(g92)
    c: Horizontal(g91)
    c: Horizontal(g82)
    c: Horizontal(g83)
    c: Horizontal(g78)
    c: Horizontal(g77)
    c: Horizontal(g154)
    c: Horizontal(g162)
    c: Horizontal(g189)
    c: Horizontal(g177)
    c: Horizontal(g163)
    c: Horizontal(g155)
    c: Horizontal(g214)
    c: Horizontal(g202)
    c: Horizontal(g192)
    c: Horizontal(g186)
    c: Horizontal(g182)
    c: Horizontal(g172)
    c: Horizontal(g211)
    c: Horizontal(g217)
    c: Horizontal(g207)
    c: Horizontal(g197)
    c: Vertical(g18,g44)
    c: Vertical(g15,g26)
    c: Vertical(g26,g43)
    c: Vertical(g43,g42)
    c: Vertical(g42,g27)
    c: Vertical(g27,g77)
    c: Vertical(g77,g90)
    c: Vertical(g90,g89)
    c: Vertical(g89,g78)
    c: Horizontal(g16,g18)
    c: Horizontal(g18,g37)
    c: Horizontal(g37,g17)
    c: Horizontal(g17,g22)
    c: Horizontal(g22,g24)
    c: Horizontal(g24,g38)
    c: Horizontal(g38,g23)
    c: Horizontal(g23,g47)
    c: Horizontal(g47,g49)
    c: Horizontal(g49,g68)
    c: Horizontal(g68,g48)
    c: Horizontal(g48,g53)
    c: Horizontal(g53,g55)
    c: Horizontal(g55,g69)
    c: Horizontal(g69,g54)
    c: Horizontal(g54,g110)
    c: Horizontal(g110,g112)
    c: Horizontal(g112,g131)
    c: Horizontal(g131,g111)
    c: Horizontal(g111,g116)
    c: Horizontal(g116,g118)
    c: Horizontal(g118,g132)
    c: Horizontal(g132,g117)
    c: DistanceX(g16,g17) = 14
    c: Equal(g37,g24)
    c: Equal(g38,g49)
    c: Equal(g68,g55)
    c: Equal(g69,g112)
    c: Equal(g131,g118)
    c: Equal(g132,g133)
    c: Equal(g133,g119)
    c: Equal(g119,g113)
    c: Equal(g113,g139)
    c: Equal(g139,g70)
    c: Equal(g70,g56)
    c: Equal(g56,g50)
    c: Equal(g50,g76)
    c: Equal(g221,g25)
    c: Equal(g25,g19)
    c: Equal(g44,g43)
    c: Equal(g43,g30)
    c: Equal(g30,g35)
    c: Equal(g35,g39)
    c: Equal(g39,g75)
    c: Equal(g75,g61)
    c: Equal(g61,g66)
    c: Equal(g66,g71)
    c: Equal(g71,g138)
    c: Equal(g138,g124)
    c: Equal(g124,g129)
    c: Equal(g129,g134)
    c: Equal(g134,g130)
    c: Equal(g130,g135)
    c: Equal(g135,g136)
    c: Equal(g136,g137)
    c: Equal(g137,g67)
    c: Equal(g67,g72)
    c: Equal(g72,g73)
    c: Equal(g73,g74)
    c: Equal(g74,g36)
    c: Equal(g36,g40)
    c: Equal(g40,g41)
    c: Equal(g41,g42)
    c: Equal(g42,g90)
    c: Equal(g90,g81)
    c: Equal(g81,g106)
    c: Equal(g106,g107)
    c: Equal(g107,g105)
    c: Equal(g105,g95)
    c: Equal(g95,g100)
    c: Equal(g100,g219)
    c: Equal(g219,g220)
    c: Equal(g220,g144)
    c: Equal(g144,g149)
    c: Equal(g149,g194)
    c: Equal(g194,g150)
    c: Equal(g150,g151)
    c: Equal(g151,g193)
    c: Equal(g193,g191)
    c: Equal(g191,g190)
    c: Equal(g190,g188)
    c: Equal(g188,g166)
    c: Equal(g166,g152)
    c: Equal(g152,g187)
    c: Equal(g187,g185)
    c: Equal(g185,g153)
    c: Equal(g153,g169)
    c: Equal(g169,g101)
    c: Equal(g101,g160)
    c: Equal(g160,g158)
    c: Equal(g158,g102)
    c: Equal(g102,g103)
    c: Equal(g103,g104)
    c: Equal(g104,g86)
    c: Equal(g86,g87)
    c: Equal(g87,g88)
    c: Equal(g88,g89)
    c: Equal(g89,g161)
    c: Equal(g161,g159)
    c: Equal(g159,g168)
    c: Equal(g168,g167)
    c: Equal(g167,g183)
    c: Equal(g183,g181)
    c: Equal(g181,g178)
    c: Equal(g178,g176)
    c: Equal(g176,g173)
    c: Equal(g173,g170)
    c: Equal(g170,g210)
    c: Equal(g210,g212)
    c: Equal(g212,g213)
    c: Equal(g213,g215)
    c: Equal(g215,g216)
    c: Equal(g216,g218)
    c: Equal(g218,g208)
    c: Equal(g208,g206)
    c: Equal(g206,g203)
    c: Equal(g203,g201)
    c: Equal(g201,g198)
    c: Equal(g198,g195)
    c: Tangent(g14,g37) = 1.5708
    c: Equal(g14,g16)
    c: Equal(g15,g22)
    c: Equal(g22,g20)
    c: Equal(g20,g21)
    c: Equal(g23,g47)
    c: Equal(g47,g46)
    c: Equal(g48,g53)
    c: Equal(g53,g52)
    c: Equal(g51,g108)
    c: Equal(g108,g110)
    c: Equal(g109,g116)
    c: Equal(g116,g114)
    c: Equal(g115,g28)
    c: Equal(g28,g26)
    c: Equal(g26,g29)
    c: Equal(g29,g27)
    c: Equal(g27,g33)
    c: Equal(g33,g31)
    c: Equal(g31,g34)
    c: Equal(g34,g32)
    c: Equal(g32,g59)
    c: Equal(g59,g57)
    c: Equal(g57,g60)
    c: Equal(g60,g58)
    c: Equal(g58,g64)
    c: Equal(g64,g62)
    c: Equal(g62,g65)
    c: Equal(g65,g63)
    c: Equal(g63,g122)
    c: Equal(g122,g120)
    c: Equal(g120,g123)
    c: Equal(g123,g121)
    c: Equal(g121,g127)
    c: Equal(g127,g125)
    c: Equal(g125,g128)
    c: Equal(g128,g126)
    c: Equal(g126,g145)
    c: Equal(g145,g148)
    c: Equal(g148,g146)
    c: Equal(g146,g147)
    c: Equal(g147,g143)
    c: Equal(g143,g140)
    c: Equal(g140,g142)
    c: Equal(g142,g141)
    c: Equal(g141,g99)
    c: Equal(g99,g96)
    c: Equal(g96,g98)
    c: Equal(g98,g97)
    c: Equal(g97,g91)
    c: Equal(g91,g94)
    c: Equal(g94,g92)
    c: Equal(g92,g93)
    c: Equal(g93,g85)
    c: Equal(g85,g83)
    c: Equal(g83,g84)
    c: Equal(g84,g82)
    c: Equal(g82,g80)
    c: Equal(g80,g77)
    c: Equal(g77,g79)
    c: Equal(g79,g78)
    c: Equal(g78,g156)
    c: Equal(g156,g154)
    c: Equal(g154,g157)
    c: Equal(g157,g155)
    c: Equal(g155,g164)
    c: Equal(g164,g162)
    c: Equal(g162,g165)
    c: Equal(g165,g163)
    c: Equal(g163,g184)
    c: Equal(g184,g180)
    c: Equal(g180,g189)
    c: Equal(g189,g179)
    c: Equal(g179,g177)
    c: Equal(g177,g175)
    c: Equal(g175,g174)
    c: Equal(g174,g171)
    c: Equal(g171,g214)
    c: Equal(g214,g202)
    c: Equal(g202,g209)
    c: Equal(g209,g205)
    c: Equal(g205,g204)
    c: Equal(g204,g200)
    c: Equal(g200,g199)
    c: Equal(g199,g196)
    c: Radius(g222) = 4.75
    c: DistanceX(g17,g22) = 5.05
    c: Vertical(g17,g29)
    c: Vertical(g29,g29)
    c: Vertical(g29,g80)
    c: Vertical(g80,g80)
    c: Vertical(g22,g33)
    c: Vertical(g33,g33)
    c: Vertical(g33,g84)
    c: Vertical(g84,g84)
    c: DistanceY(g26,g15) = 5.05
    c: Horizontal(g26,g31)
    c: Horizontal(g31,g57)
    c: Horizontal(g57,g62)
    c: Horizontal(g62,g120)
    c: Horizontal(g120,g125)
    c: Tangent(g17,g37) = 1.5708
    c: Tangent(g17,g19) = 1.5708
    c: Tangent(g15,g19) = -1.5708
    c: Tangent(g15,g44) = -1.5708
    c: Tangent(g16,g44) = -1.5708
    c: DistanceX(g23,g47) = 5.05
    c: Vertical(g23,g34)
    c: Vertical(g34,g34)
    c: Vertical(g34,g85)
    c: Vertical(g85,g85)
    c: Vertical(g47,g59)
    c: Vertical(g59,g59)
    c: Vertical(g59,g93)
    c: Vertical(g93,g93)
    c: DistanceY(g77,g27) = 5.05
    c: Horizontal(g27,g32)
    c: Horizontal(g32,g58)
    c: Horizontal(g58,g63)
    c: Horizontal(g63,g121)
    c: Horizontal(g121,g126)
    c: Horizontal(g77,g82)
    c: Horizontal(g82,g91)
    c: Horizontal(g91,g96)
    c: Horizontal(g96,g140)
    c: Horizontal(g140,g145)
    c: DistanceX(g48,g53) = 5.05
    c: Vertical(g48,g60)
    c: Vertical(g60,g60)
    c: Vertical(g60,g94)
    c: Vertical(g94,g94)
    c: Vertical(g53,g64)
    c: Vertical(g64,g98)
    c: Vertical(g98,g98)
    c: Vertical(g98,g156)
    c: Vertical(g156,g156)
    c: DistanceX(g54,g110) = 5.05
    c: Vertical(g65,g65)
    c: Vertical(g65,g99)
    c: Vertical(g99,g99)
    c: Vertical(g99,g157)
    c: Vertical(g157,g157)
    c: Vertical(g110,g122)
    c: Vertical(g122,g122)
    c: Vertical(g122,g142)
    c: Vertical(g142,g142)
    c: Vertical(g142,g164)
    c: Vertical(g164,g164)
    c: DistanceY(g154,g97) = 5.05
    c: Horizontal(g78,g83)
    c: Horizontal(g83,g92)
    c: Horizontal(g92,g97)
    c: Horizontal(g97,g141)
    c: Horizontal(g141,g146)
    c: Horizontal(g154,g162)
    c: Horizontal(g162,g192)
    c: Horizontal(g191,g189)
    c: Horizontal(g188,g186)
    c: DistanceX(g111,g116) = 5.05
    c: Vertical(g123,g123)
    c: Vertical(g123,g143)
    c: Vertical(g143,g143)
    c: Vertical(g143,g165)
    c: Vertical(g165,g165)
    c: Vertical(g116,g127)
    c: Vertical(g127,g147)
    c: Vertical(g147,g147)
    c: DistanceY(g210,g170) = 5.05
    c: Horizontal(g172,g176)
    c: Horizontal(g177,g181)
    c: Horizontal(g182,g163)
    c: Horizontal(g163,g155)
    c: Horizontal(g211,g213)
    c: Horizontal(g214,g216)
    c: DistanceX(g165,g179) = 12.19
    c: Vertical(g179,g178)
    c: Vertical(g178,g204)
    c: Vertical(g204,g203)
    c: DistanceX(g180,g179) = 2.75
    c: Vertical(g180,g180)
    c: Vertical(g180,g205)
    c: Vertical(g205,g205)
    c: DistanceX(g184,g180) = 2
    c: Equal(g192,g186)
    c: Equal(g186,g172)
    c: Equal(g172,g182)
    c: Equal(g182,g217)
    c: Equal(g217,g211)
    c: Equal(g211,g197)
    c: Equal(g197,g207)
    c: DistanceX(g175,g174) = 2.75
    c: Vertical(g175,g175)
    c: Vertical(g175,g200)
    c: Vertical(g200,g200)
    c: Vertical(g198,g199)
    c: Vertical(g199,g173)
    c: Vertical(g173,g174)
    c: Tangent(g22,g24) = -1.5708
    c: Tangent(g20,g24) = 1.5708
    c: Tangent(g20,g38) = 1.5708
    c: Tangent(g23,g38) = 1.5708
    c: Tangent(g23,g221) = 1.5708
    c: Tangent(g21,g221) = -1.5708
    c: Tangent(g21,g25) = -1.5708
    c: Tangent(g22,g25) = -1.5708
    c: Tangent(g47,g49) = -1.5708
    c: Tangent(g45,g49) = 1.5708
    c: Tangent(g45,g68) = 1.5708
    c: Tangent(g48,g68) = 1.5708
    c: Tangent(g48,g50) = 1.5708
    c: Tangent(g46,g50) = -1.5708
    c: Tangent(g46,g76) = -1.5708
    c: Tangent(g47,g76) = -1.5708
    c: Tangent(g53,g55) = -1.5708
    c: Tangent(g51,g55) = 1.5708
    c: Tangent(g51,g69) = 1.5708
    c: Tangent(g54,g69) = 1.5708
    c: Tangent(g54,g70) = 1.5708
    c: Tangent(g52,g70) = -1.5708
    c: Tangent(g52,g56) = -1.5708
    c: Tangent(g53,g56) = -1.5708
    c: Tangent(g110,g112) = -1.5708
    c: Tangent(g108,g112) = 1.5708
    c: Tangent(g108,g131) = 1.5708
    c: Tangent(g111,g131) = 1.5708
    c: Tangent(g111,g113) = 1.5708
    c: Tangent(g109,g113) = -1.5708
    c: Tangent(g109,g139) = -1.5708
    c: Tangent(g110,g139) = -1.5708
    c: Tangent(g116,g118) = -1.5708
    c: Tangent(g114,g118) = 1.5708
    c: Tangent(g114,g132) = 1.5708
    c: Tangent(g117,g132) = 1.5708
    c: Tangent(g117,g133) = 1.5708
    c: Tangent(g115,g133) = -1.5708
    c: Tangent(g115,g119) = -1.5708
    c: Tangent(g116,g119) = -1.5708
    c: Tangent(g128,g134) = 1.5708
    c: Tangent(g125,g134) = 1.5708
    c: Tangent(g125,g129) = 1.5708
    c: Tangent(g127,g129) = -1.5708
    c: Tangent(g127,g135) = -1.5708
    c: Tangent(g126,g135) = -1.5708
    c: Tangent(g126,g130) = -1.5708
    c: Tangent(g128,g130) = 1.5708
    c: Tangent(g123,g124) = 1.5708
    c: Tangent(g120,g124) = 1.5708
    c: Tangent(g120,g138) = 1.5708
    c: Tangent(g122,g138) = -1.5708
    c: Tangent(g65,g71) = 1.5708
    c: Tangent(g62,g71) = 1.5708
    c: Tangent(g62,g66) = 1.5708
    c: Tangent(g64,g66) = -1.5708
    c: Tangent(g64,g72) = -1.5708
FEATURE [PartDesign::Body] Body
  Group = -> [Sketch003]
  Origin = -> Origin004
FEATURE [App::Part] Part  label="switch.plate"
  Group = -> [Body]
  Origin = -> Origin003
